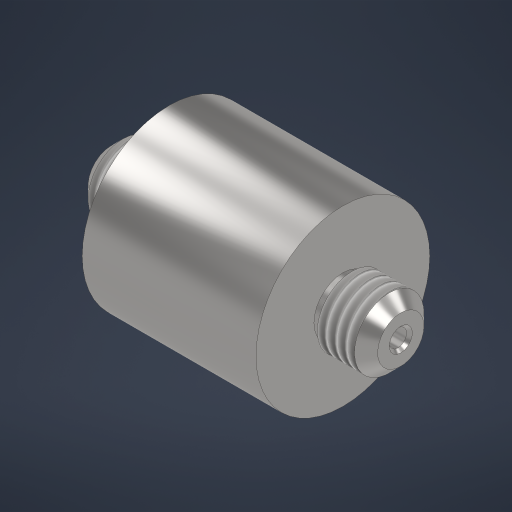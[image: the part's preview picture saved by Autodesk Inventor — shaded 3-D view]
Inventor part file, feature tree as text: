
AUTODESK INVENTOR PART (.ipt)
format: ipt  version: 2024.3 (Build 283343000, 343)  size: 288,768 bytes
history: native  units: mm
features: sketch x2, revolve x2, chamfer x2, thread x1, hole x1
ambient origin geometry x8: Origin, YZ Plane, XZ Plane, XY Plane, X Axis, Y Axis, Z Axis, Center Point
bodies: Solid1 (feature_tree)
feature tree (8):
  sketch  "Sketch1"  dims[d0=30.0mm d1=12.0mm]
  revolve  "Revolution1"  [1 undecoded]
  revolve  "Revolution2"  Angle=60.0deg
  thread  "Thread2"  [1 undecoded]
  chamfer  "Chamfer1"  Distance=30.0mm
  chamfer  "Chamfer2"  Distance=50.0mm
  hole  "Hole1"  [1 undecoded]
  sketch  "Sketch2"  dims[d3=8.42265mm d5=60.0deg d6=10.0mm d7=30.0mm d8=50.0mm d9=10.297443mm d10=10.0mm d11=4.0mm d12=18.0mm d13=23.0mm d14=360.0deg d15=90.0deg d18=50.0mm d19=0.0mm d20=2.0mm d21=2.0mm d22=45.0deg d23=3.0mm d24=0.5mm d25=2.0mm d26=45.0deg d27=10.0mm d29=1.0mm d30=10.106mm d31=16.0mm d32=13.0mm d33=2.0mm d34=90.0deg d35=20.0mm d36=20.594885mm]
note: 3 required parameter values undecoded (feature->parameter linkage not recoverable at this tier; creation-order binding heuristic only, values carry confidence <= 0.55)